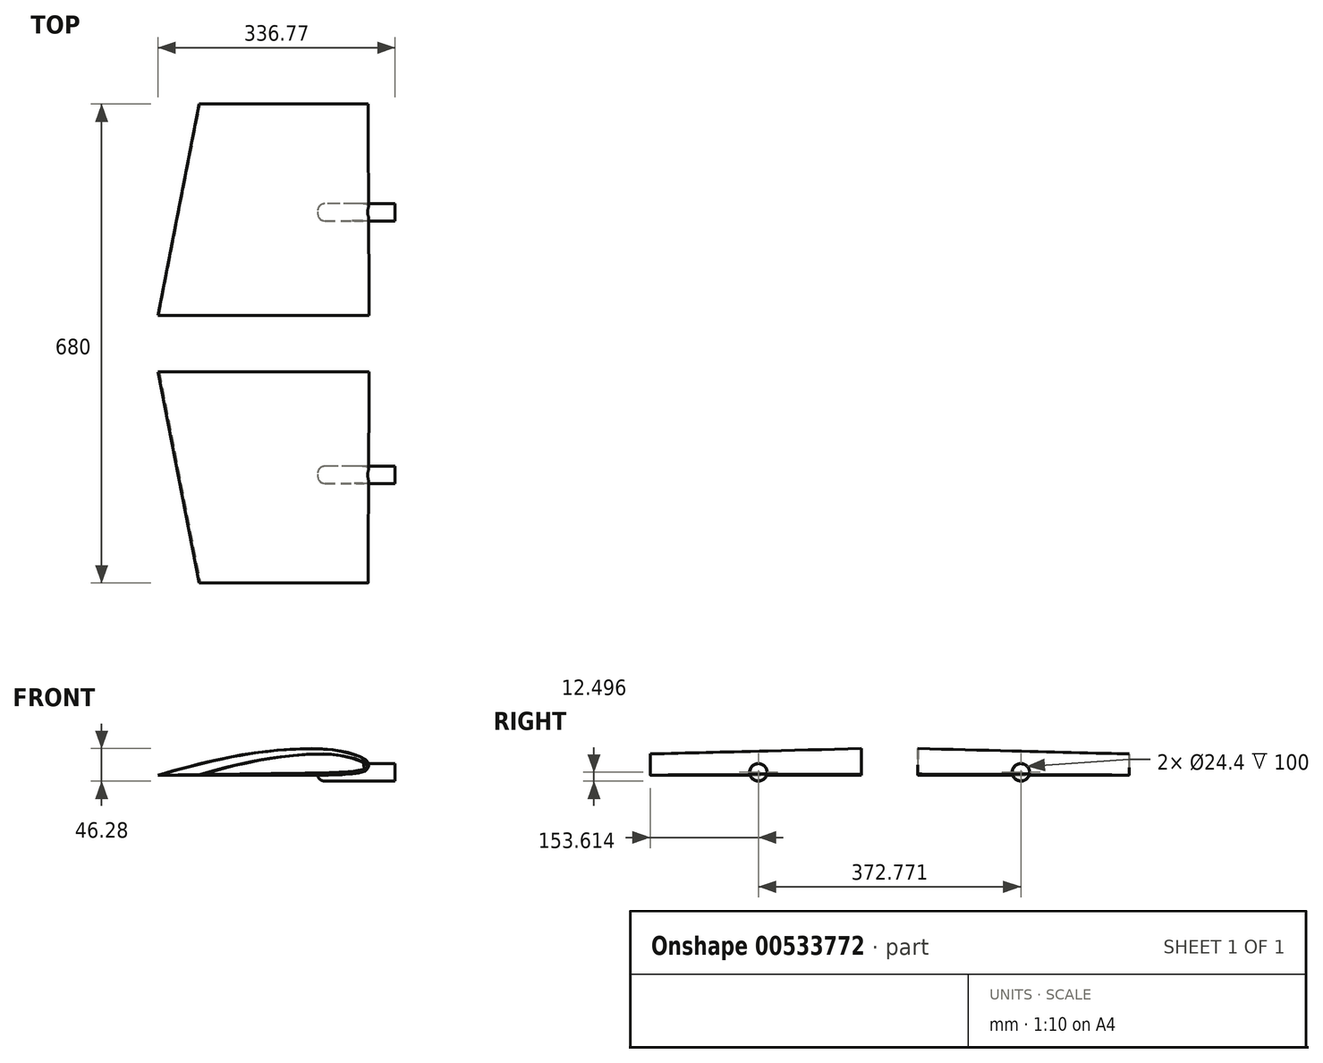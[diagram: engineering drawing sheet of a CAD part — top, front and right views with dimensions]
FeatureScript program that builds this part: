
annotation { "Feature Type Name" : "Feature", "Feature Type Description" : "" }
export const myFeature = defineFeature(function(context is Context, id is Id, definition is map)
    precondition{}
    {
        {
            var Q0;
            Q0=qCreatedBy(makeId("Front.planeOp"),FACE);
            var sketch = newSketch(context, id + "F0", { "sketchPlane" : qUnion([Q0])});
            skFitSpline(sketch, "E0.0.0", {"points": [v(153.23, 36.43) * mm, v(153.28, 36.78) * mm, v(153.3, 37.5) * mm, v(153.01, 38.58) * mm, v(152.5, 39.62) * mm, v(151.78, 40.62) * mm, v(150.94, 41.56) * mm, v(150, 42.45) * mm, v(148.99, 43.29) * mm, v(147.57, 44.34) * mm, v(145.72, 45.55) * mm, v(143.46, 46.85) * mm, v(141.58, 47.8) * mm, v(140.1, 48.48) * mm, v(139, 48.96) * mm, v(137.91, 49.4) * mm, v(136.83, 49.82) * mm, v(135.74, 50.22) * mm, v(134.65, 50.6) * mm, v(133.55, 50.97) * mm, v(132.06, 51.46) * mm, v(130.16, 52.06) * mm, v(127.82, 52.76) * mm, v(125.45, 53.45) * mm, v(123.07, 54.1) * mm, v(120.68, 54.72) * mm, v(118.3, 55.3) * mm, v(115.93, 55.82) * mm, v(113.57, 56.3) * mm, v(111.2, 56.74) * mm, v(108.82, 57.15) * mm, v(105.63, 57.64) * mm, v(101.61, 58.2) * mm, v(96.76, 58.72) * mm, v(91.92, 59.12) * mm, v(87.08, 59.4) * mm, v(82.23, 59.6) * mm, v(77.37, 59.73) * mm, v(70.89, 59.82) * mm, v(64.41, 59.79) * mm, v(57.94, 59.66) * mm, v(53.08, 59.5) * mm, v(48.23, 59.31) * mm, v(43.38, 59.07) * mm, v(38.53, 58.78) * mm, v(32.07, 58.34) * mm, v(24, 57.67) * mm, v(15.95, 56.87) * mm, v(9.5, 56.15) * mm, v(4.68, 55.57) * mm, v(-0.14, 54.96) * mm, v(-6.56, 54.09) * mm, v(-14.56, 52.9) * mm, v(-22.55, 51.62) * mm, v(-28.93, 50.52) * mm, v(-33.71, 49.67) * mm, v(-38.49, 48.78) * mm, v(-44.84, 47.56) * mm, v(-52.74, 45.98) * mm, v(-60.62, 44.3) * mm, v(-66.94, 42.9) * mm, v(-71.68, 41.83) * mm, v(-76.4, 40.73) * mm, v(-81.12, 39.62) * mm, v(-85.83, 38.48) * mm, v(-89.75, 37.51) * mm, v(-92.9, 36.73) * mm, v(-96.04, 35.94) * mm, v(-101.54, 34.53) * mm, v(-107.04, 33.1) * mm, v(-111.74, 31.84) * mm, v(-114.08, 31.2) * mm, v(-116.43, 30.57) * mm, v(-118.78, 29.92) * mm, v(-121.15, 29.27) * mm, v(-123.52, 28.61) * mm, v(-125.88, 27.95) * mm, v(-128.22, 27.29) * mm, v(-130.56, 26.62) * mm, v(-132.89, 25.94) * mm, v(-135.2, 25.26) * mm, v(-138.3, 24.34) * mm, v(-142.15, 23.17) * mm, v(-145.23, 22.2) * mm, v(-146.77, 21.7) * mm]});
            skFitSpline(sketch, "E0.0.1", {"points": [v(-146.77, 21.7) * mm, v(-145.18, 21.69) * mm, v(-141.98, 21.67) * mm, v(-137.18, 21.68) * mm, v(-132.43, 21.7) * mm, v(-127.71, 21.76) * mm, v(-122.96, 21.83) * mm, v(-118.16, 21.9) * mm, v(-113.36, 21.97) * mm, v(-108.57, 22.04) * mm, v(-104.57, 22.1) * mm, v(-101.37, 22.15) * mm, v(-98.97, 22.19) * mm, v(-96.58, 22.23) * mm, v(-94.22, 22.26) * mm, v(-91.9, 22.3) * mm, v(-89.66, 22.33) * mm, v(-87.46, 22.37) * mm, v(-84.57, 22.4) * mm, v(-81.72, 22.45) * mm, v(-78.8, 22.5) * mm, v(-76.57, 22.53) * mm, v(-74.28, 22.56) * mm, v(-71.93, 22.6) * mm, v(-69.94, 22.62) * mm, v(-68.34, 22.65) * mm, v(-66.74, 22.67) * mm, v(-64.74, 22.7) * mm, v(-61.54, 22.74) * mm, v(-57.55, 22.8) * mm, v(-52.75, 22.87) * mm, v(-48.75, 22.93) * mm, v(-45.55, 22.98) * mm, v(-43.15, 23) * mm, v(-40.76, 23.04) * mm, v(-38.36, 23.08) * mm, v(-35.96, 23.11) * mm, v(-33.61, 23.15) * mm, v(-31.34, 23.18) * mm, v(-29.13, 23.21) * mm, v(-26.99, 23.25) * mm, v(-24.2, 23.29) * mm, v(-21.43, 23.33) * mm, v(-18.6, 23.37) * mm, v(-16.43, 23.4) * mm, v(-14.18, 23.43) * mm, v(-11.86, 23.47) * mm, v(-9.88, 23.5) * mm, v(-8.28, 23.52) * mm, v(-6.68, 23.54) * mm, v(-4.68, 23.57) * mm, v(-1.48, 23.62) * mm, v(2.52, 23.67) * mm, v(7.31, 23.74) * mm, v(13.7, 23.84) * mm, v(21.7, 23.95) * mm, v(31.3, 24.09) * mm, v(40.9, 24.22) * mm, v(50.49, 24.36) * mm, v(60.08, 24.5) * mm, v(68.07, 24.61) * mm, v(74.47, 24.72) * mm, v(79.27, 24.8) * mm, v(84.06, 24.89) * mm, v(88.85, 24.99) * mm, v(92.83, 25.1) * mm, v(96.03, 25.2) * mm, v(98.44, 25.28) * mm, v(100.85, 25.37) * mm, v(103.25, 25.47) * mm, v(105.65, 25.57) * mm, v(108.03, 25.67) * mm, v(110.41, 25.78) * mm, v(112.79, 25.9) * mm, v(115.18, 26.04) * mm, v(117.57, 26.2) * mm, v(120, 26.4) * mm, v(122.42, 26.62) * mm, v(124.85, 26.86) * mm, v(127.26, 27.1) * mm, v(129.63, 27.33) * mm, v(131.95, 27.55) * mm, v(134.23, 27.78) * mm, v(136.51, 28.05) * mm, v(138.45, 28.35) * mm, v(140.04, 28.66) * mm, v(141.65, 29.02) * mm, v(143.7, 29.57) * mm, v(146.15, 30.41) * mm, v(148.13, 31.29) * mm, v(149.62, 32.12) * mm, v(150.66, 32.81) * mm, v(151.6, 33.59) * mm, v(152.38, 34.45) * mm, v(152.96, 35.4) * mm, v(153.17, 36.08) * mm, v(153.23, 36.43) * mm]});
            skLineSegment(sketch, "E1", {"start": v(-6.55, 23.54) * mm, "end": v(8.44, 54.12) * mm});
            skLineSegment(sketch, "E2", {"start": v(8.44, 54.12) * mm, "end": v(8.44, 23.76) * mm});
            skSolve(sketch);
        }
        {
            var Q0;
            Q0=qCreatedBy(makeId("Front.planeOp"),FACE);
            cPlane(context, id + "F1", {"entities" : qUnion([Q0]), "cplaneType" : CPlaneType.OFFSET, "offset" : 300 * mm, "width" : 150 * mm, "height" : 150 * mm});
        }
        {
            var Q0;
            Q0=qCreatedBy(id+"F1.planeOp",FACE);
            var sketch = newSketch(context, id + "F2", { "sketchPlane" : qUnion([Q0])});
            skFitSpline(sketch, "E3.0.0", {"points": [v(151.57, 32.51) * mm, v(151.6, 32.87) * mm, v(151.58, 33.58) * mm, v(151.25, 34.65) * mm, v(150.67, 35.66) * mm, v(149.92, 36.62) * mm, v(149.03, 37.52) * mm, v(148.04, 38.36) * mm, v(147, 39.14) * mm, v(145.52, 40.13) * mm, v(143.61, 41.25) * mm, v(141.29, 42.42) * mm, v(139.37, 43.28) * mm, v(137.85, 43.88) * mm, v(136.73, 44.3) * mm, v(135.62, 44.7) * mm, v(134.52, 45.06) * mm, v(133.41, 45.4) * mm, v(132.3, 45.73) * mm, v(131.18, 46.05) * mm, v(129.67, 46.46) * mm, v(127.74, 46.96) * mm, v(125.37, 47.54) * mm, v(122.97, 48.1) * mm, v(120.56, 48.64) * mm, v(118.14, 49.14) * mm, v(115.73, 49.6) * mm, v(113.34, 50) * mm, v(110.96, 50.36) * mm, v(108.57, 50.68) * mm, v(106.18, 50.96) * mm, v(102.97, 51.3) * mm, v(98.92, 51.64) * mm, v(94.05, 51.93) * mm, v(89.2, 52.09) * mm, v(84.35, 52.13) * mm, v(79.5, 52.08) * mm, v(74.63, 51.96) * mm, v(68.16, 51.72) * mm, v(61.69, 51.36) * mm, v(55.23, 50.9) * mm, v(50.39, 50.51) * mm, v(45.55, 50.07) * mm, v(40.72, 49.59) * mm, v(35.89, 49.05) * mm, v(29.46, 48.28) * mm, v(21.44, 47.22) * mm, v(13.43, 46.01) * mm, v(7.04, 44.97) * mm, v(2.25, 44.14) * mm, v(-2.53, 43.29) * mm, v(-8.9, 42.1) * mm, v(-16.84, 40.51) * mm, v(-24.75, 38.82) * mm, v(-31.07, 37.4) * mm, v(-35.8, 36.3) * mm, v(-40.53, 35.18) * mm, v(-46.8, 33.65) * mm, v(-54.61, 31.66) * mm, v(-62.4, 29.6) * mm, v(-68.64, 27.88) * mm, v(-73.32, 26.57) * mm, v(-77.99, 25.23) * mm, v(-82.64, 23.88) * mm, v(-87.29, 22.5) * mm, v(-91.16, 21.35) * mm, v(-94.26, 20.4) * mm, v(-97.35, 19.46) * mm, v(-102.77, 17.78) * mm, v(-108.2, 16.06) * mm, v(-112.83, 14.57) * mm, v(-115.14, 13.82) * mm, v(-117.45, 13.07) * mm, v(-119.77, 12.3) * mm, v(-122.1, 11.53) * mm, v(-124.43, 10.75) * mm, v(-126.76, 9.97) * mm, v(-129.06, 9.2) * mm, v(-131.36, 8.41) * mm, v(-133.65, 7.62) * mm, v(-135.94, 6.82) * mm, v(-138.97, 5.75) * mm, v(-142.76, 4.38) * mm, v(-145.8, 3.25) * mm, v(-147.3, 2.68) * mm]});
            skFitSpline(sketch, "E3.0.1", {"points": [v(-148.63, 22.5) * mm, v(-147.03, 22.46) * mm, v(-143.83, 22.39) * mm, v(-139.03, 22.32) * mm, v(-134.29, 22.28) * mm, v(-129.56, 22.26) * mm, v(-124.81, 22.25) * mm, v(-120.01, 22.24) * mm, v(-115.22, 22.24) * mm, v(-110.42, 22.24) * mm, v(-106.42, 22.23) * mm, v(-103.22, 22.23) * mm, v(-100.82, 22.23) * mm, v(-98.43, 22.23) * mm, v(-96.07, 22.23) * mm, v(-93.76, 22.23) * mm, v(-91.51, 22.23) * mm, v(-89.31, 22.23) * mm, v(-86.42, 22.23) * mm, v(-83.57, 22.22) * mm, v(-80.65, 22.22) * mm, v(-78.41, 22.22) * mm, v(-76.12, 22.22) * mm, v(-73.78, 22.21) * mm, v(-71.79, 22.2) * mm, v(-70.19, 22.2) * mm, v(-68.59, 22.2) * mm, v(-66.59, 22.2) * mm, v(-63.39, 22.2) * mm, v(-59.4, 22.2) * mm, v(-54.6, 22.19) * mm, v(-50.6, 22.18) * mm, v(-47.4, 22.18) * mm, v(-45, 22.18) * mm, v(-42.6, 22.17) * mm, v(-40.2, 22.17) * mm, v(-37.8, 22.17) * mm, v(-35.46, 22.17) * mm, v(-33.18, 22.16) * mm, v(-30.97, 22.16) * mm, v(-28.83, 22.16) * mm, v(-26.03, 22.16) * mm, v(-23.28, 22.15) * mm, v(-20.45, 22.15) * mm, v(-18.27, 22.15) * mm, v(-16.02, 22.15) * mm, v(-13.7, 22.14) * mm, v(-11.72, 22.14) * mm, v(-10.12, 22.14) * mm, v(-8.52, 22.14) * mm, v(-6.52, 22.13) * mm, v(-3.32, 22.13) * mm, v(0.68, 22.12) * mm, v(5.47, 22.12) * mm, v(11.87, 22.11) * mm, v(19.87, 22.1) * mm, v(29.46, 22.08) * mm, v(39.06, 22.07) * mm, v(48.65, 22.06) * mm, v(58.25, 22.04) * mm, v(66.24, 22.03) * mm, v(72.64, 22.04) * mm, v(77.44, 22.05) * mm, v(82.23, 22.06) * mm, v(87.02, 22.08) * mm, v(91, 22.12) * mm, v(94.2, 22.18) * mm, v(96.61, 22.22) * mm, v(99.02, 22.28) * mm, v(101.43, 22.34) * mm, v(103.83, 22.4) * mm, v(106.21, 22.46) * mm, v(108.6, 22.53) * mm, v(110.97, 22.62) * mm, v(113.36, 22.72) * mm, v(115.76, 22.85) * mm, v(118.18, 23) * mm, v(120.62, 23.2) * mm, v(123.05, 23.39) * mm, v(125.46, 23.59) * mm, v(127.83, 23.78) * mm, v(130.15, 23.97) * mm, v(132.44, 24.16) * mm, v(134.73, 24.4) * mm, v(136.67, 24.66) * mm, v(138.26, 24.95) * mm, v(139.88, 25.28) * mm, v(141.93, 25.8) * mm, v(144.4, 26.6) * mm, v(146.4, 27.45) * mm, v(147.9, 28.25) * mm, v(148.95, 28.93) * mm, v(149.9, 29.7) * mm, v(150.7, 30.54) * mm, v(151.29, 31.48) * mm, v(151.5, 32.16) * mm, v(151.57, 32.51) * mm]});
            skLineSegment(sketch, "E4", {"start": v(-4.36, 22.13) * mm, "end": v(11.02, 43.14) * mm});
            skLineSegment(sketch, "E5", {"start": v(11.02, 43.14) * mm, "end": v(11.02, 22.11) * mm});
            skSolve(sketch);
        }
        {
            var Q0;
            Q0=makeQuery(id+"F0.imprint","IMPRINT",FACE,{"disambiguationData":[TD([[makeQuery(id+"F0.imprint","IMPRINT",EDGE,{"derivedFrom":sQuery(id+"F0.wireOp",EDGE,"E0.0.0")}),1.0]])]});
            var Q1;
            Q1=makeQuery(id+"F2.imprint","IMPRINT",FACE,{"disambiguationData":[TD([[makeQuery(id+"F2.imprint","IMPRINT",EDGE,{"derivedFrom":sQuery(id+"F2.wireOp",EDGE,"E3.0.0")}),1.0]])]});
            loft(context, id + "F3", {"sheetProfilesArray" : [{ "sheetProfileEntities" : qUnion([Q0]) }, { "sheetProfileEntities" : qUnion([Q1]) }]});
        }
        {
            var Q0;
            Q0=qCreatedBy(makeId("Front.planeOp"),FACE);
            cPlane(context, id + "F4", {"entities" : qUnion([Q0]), "cplaneType" : CPlaneType.OFFSET, "offset" : 40 * mm, "oppositeDirection" : true, "width" : 150 * mm, "height" : 150 * mm});
        }
        {
            var Q0;
            Q0=makeQuery(id+"F3.opLoft","SWEPT_BODY",BODY,{"disambiguationData":[OSD([makeQuery(id+"F0.imprint","IMPRINT",FACE,{"disambiguationData":[TD([[makeQuery(id+"F0.imprint","IMPRINT",EDGE,{"derivedFrom":sQuery(id+"F0.wireOp",EDGE,"E0.0.0")}),1.0]])]}),makeQuery(id+"F2.imprint","IMPRINT",FACE,{"disambiguationData":[TD([[makeQuery(id+"F2.imprint","IMPRINT",EDGE,{"derivedFrom":sQuery(id+"F2.wireOp",EDGE,"E3.0.0")}),1.0]])]})])]});
            var Q1;
            Q1=qCreatedBy(id+"F4.planeOp",FACE);
            mirror(context, id + "F5", {"entities" : qUnion([Q0]), "mirrorPlane" : qUnion([Q1])});
        }
        {
            var Q0;
            Q0=qCreatedBy(makeId("Right.planeOp"),FACE);
            cPlane(context, id + "F6", {"entities" : qUnion([Q0]), "cplaneType" : CPlaneType.OFFSET, "offset" : 80 * mm, "width" : 150 * mm, "height" : 150 * mm});
        }
        {
            var Q0;
            Q0=qCreatedBy(id+"F6.planeOp",FACE);
            var sketch = newSketch(context, id + "F7", { "sketchPlane" : qUnion([Q0])});
            skCircle(sketch, "E6", {"center": v(-146.39, 26.05) * mm, "radius": 12.5 * mm});
            skCircle(sketch, "E7.MirrorC", {"center": v(226.39, 26.05) * mm, "radius": 12.5 * mm});
            skSolve(sketch);
        }
        {
            var Q0;
            Q0 = qSketchRegion(id + "F7", true);
            extrude(context, id + "F8", {"entities" : qUnion([Q0]), "operationType" : NewBodyOperationType.ADD, "depth" : 110 * mm, "offsetDistance" : 25 * mm});
        }
        {
            var Q0;
            Q0=makeQuery(id+"F8.opExtrude","CAP_EDGE",EDGE,{"disambiguationData":[OSD([sQuery(id+"F7.wireOp",EDGE,"E6")])],"isStart":true});
            var Q1;
            Q1=makeQuery(id+"F8.opExtrude","CAP_EDGE",EDGE,{"disambiguationData":[OSD([sQuery(id+"F7.wireOp",EDGE,"E7.MirrorC")])],"isStart":true});
            fillet(context, id + "F9", {"entities" : qUnion([Q0, Q1]), "radius" : 10 * mm, "tangentPropagation" : true, "allowEdgeOverflow" : false});
        }
        {
            var Q0;
            {var subQ2=sQuery(id+"F2.wireOp",EDGE,"E3.0.0");Q0=makeQuery(id+"F3.opLoft","CAP_FACE",FACE,{"disambiguationData":[OSD([makeQuery(id+"F2.imprint","IMPRINT",FACE,{"disambiguationData":[TD([[makeQuery(id+"F2.imprint","IMPRINT",EDGE,{"derivedFrom":subQ2}),1.0]])]})])],"isStart":true});}
            var Q1;
            {var subQ2=sQuery(id+"F2.wireOp",EDGE,"E3.0.0");Q1=makeQuery(id+"F5.opPattern","COPY",FACE,{"derivedFrom":makeQuery(id+"F3.opLoft","CAP_FACE",FACE,{"disambiguationData":[OSD([makeQuery(id+"F2.imprint","IMPRINT",FACE,{"disambiguationData":[TD([[makeQuery(id+"F2.imprint","IMPRINT",EDGE,{"derivedFrom":subQ2}),1.0]])]})])],"isStart":true}),"instanceName":"1"});}
            var Q2;
            Q2=makeQuery(id+"F8.opExtrude","CAP_FACE",FACE,{"disambiguationData":[OSD([sQuery(id+"F7.wireOp",EDGE,"E7.MirrorC")])],"isStart":false});
            var Q3;
            Q3=makeQuery(id+"F8.opExtrude","CAP_FACE",FACE,{"disambiguationData":[OSD([sQuery(id+"F7.wireOp",EDGE,"E6")])],"isStart":false});
            shell(context, id + "F10", {"entities" : qUnion([Q0, Q1, Q2, Q3]), "thickness" : .3 * mm});
        }
    });
